# Revit family: 29003-presto
name_source: partatom
category: Plumbing Fixtures
units: mm (PartAtom-declared; Revit-internal decimal feet)

## family parameters
Always vertical = Yes
Cut with Voids When Loaded = No
Maintain Annotation Orientation = No
OmniClass Number = 23.45.00.00
OmniClass Title = Sanitary, Laundry, and Cleaning Equipment
Part Type = Normal
Room Calculation Point = No
Round Connector Dimension = Use Diameter
Shared = No
Work Plane-Based = Yes

## types (1)
- 29003- Les Robinets PRESTO
    - Hydraulic supply = 20.00 mm
    -Delivered with = 2 Filter gaskets
2 NF check valves
    > Standards & approvals = 200-hour neutral salt spray resistant (NSS) in accordance with ISO 9227 Brass body in accordance with EN 1982, EN 12164, EN 12156
    Assembly Code = 29003
    Default Elevation = 1219 mm
    Description = 2 Filter gaskets
2 NF check valves
    Minimum differential temperature = 15 °C
    Model = Thermostatic mixing valve with disconnectable temperature control
    Recommended pressure = 3.0 bar
    Stability of mixed water temperature = 2 °C
    URL = https://www.prestodatashare.com
    brand = Les Robinets PRESTO
    flow = 43.0 L/min
    material = <By Category>
    material 1 = Copper
    material 2 = chroome
    material 3 = po
    material 5 = stan
    material 6 = red
    min flow = 5.0 L/min
    min pressure = 1.0 bar
    pressure = 5.0 bar
    range = Safety Thermostatic Mixing Valve
    ref = 29003 - Thermostatic mixing valve with disconnectable temperature control
    temperature hot wotar = 80 °C

## geometry (parser evidence)
native form markers: Sweep x3
no freeform markers — native parametric forms only
